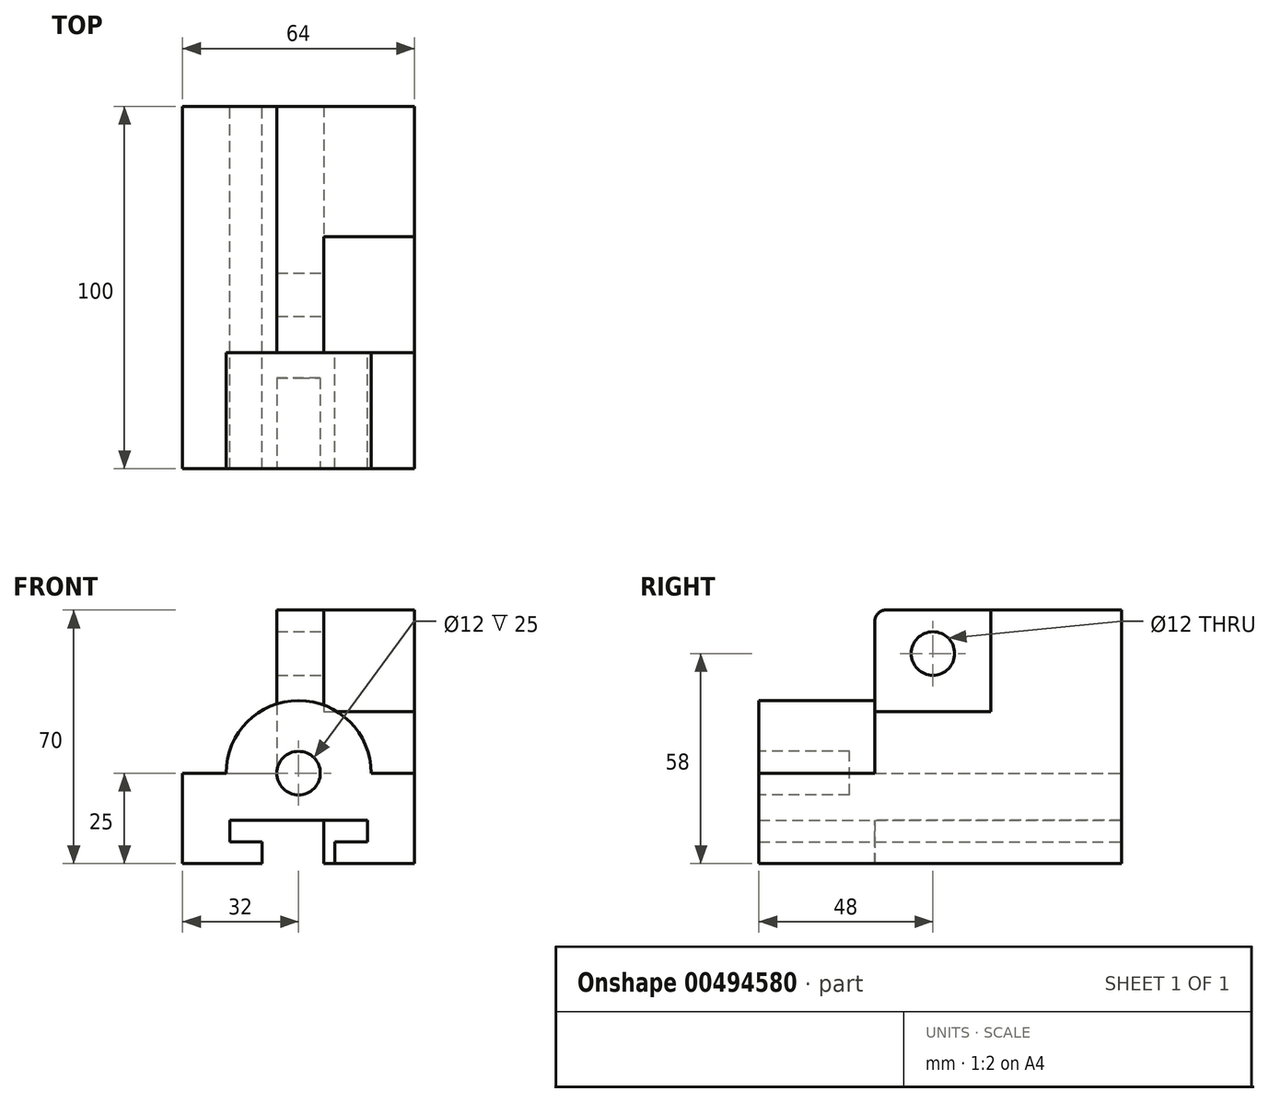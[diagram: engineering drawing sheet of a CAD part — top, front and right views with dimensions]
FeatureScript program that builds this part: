
annotation { "Feature Type Name" : "Feature", "Feature Type Description" : "" }
export const myFeature = defineFeature(function(context is Context, id is Id, definition is map)
    precondition{}
    {
        {
            var Q0;
            Q0=qCreatedBy(makeId("Front.planeOp"),FACE);
            var sketch = newSketch(context, id + "F0", { "sketchPlane" : qUnion([Q0])});
            skLineSegment(sketch, "E0.bottom", {"start": v(-32, 0) * mm, "end": v(-10, 0) * mm});
            skLineSegment(sketch, "E0.top", {"start": v(-32, 25) * mm, "end": v(32, 25) * mm});
            skLineSegment(sketch, "E0.left", {"start": v(-32, 0) * mm, "end": v(-32, 25) * mm});
            skLineSegment(sketch, "E0.right", {"start": v(32, 0) * mm, "end": v(32, 25) * mm});
            skLineSegment(sketch, "E1.left", {"start": v(-10, 0) * mm, "end": v(-10, 6) * mm});
            skLineSegment(sketch, "E1.right", {"start": v(10, 0) * mm, "end": v(10, 6) * mm});
            skLineSegment(sketch, "E2.bottom", {"start": v(19, 6) * mm, "end": v(10, 6) * mm});
            skLineSegment(sketch, "E2.top", {"start": v(19, 12) * mm, "end": v(-19, 12) * mm});
            skLineSegment(sketch, "E2.left", {"start": v(19, 6) * mm, "end": v(19, 12) * mm});
            skLineSegment(sketch, "E2.right", {"start": v(-19, 6) * mm, "end": v(-19, 12) * mm});
            skLineSegment(sketch, "E3.trimOffspring", {"start": v(-10, 6) * mm, "end": v(-19, 6) * mm});
            skLineSegment(sketch, "E4.trimOffspring", {"start": v(10, 0) * mm, "end": v(32, 0) * mm});
            skSolve(sketch);
        }
        {
            var Q0;
            Q0 = qSketchRegion(id + "F0", true);
            extrude(context, id + "F1", {"entities" : qUnion([Q0]), "endBound" : BoundingType.SYMMETRIC, "depth" : 100 * mm});
        }
        {
            var Q0;
            Q0=makeQuery(id+"F1.opExtrude","SWEPT_FACE",FACE,{"disambiguationData":[OSD([sQuery(id+"F0.wireOp",EDGE,"E0.right")])]});
            var sketch = newSketch(context, id + "F2", { "sketchPlane" : qUnion([Q0])});
            skLineSegment(sketch, "E5", {"start": v(50, 25) * mm, "end": v(50, 70) * mm});
            skLineSegment(sketch, "E6", {"start": v(50, 70) * mm, "end": v(14, 70) * mm});
            skLineSegment(sketch, "E7", {"start": v(14, 70) * mm, "end": v(14, 42) * mm});
            skLineSegment(sketch, "E8", {"start": v(14, 42) * mm, "end": v(-18, 42) * mm});
            skLineSegment(sketch, "E9", {"start": v(-18, 42) * mm, "end": v(-18, 25) * mm});
            skLineSegment(sketch, "E10", {"start": v(-18, 25) * mm, "end": v(-18, 0) * mm});
            skLineSegment(sketch, "E11", {"start": v(-18, 0) * mm, "end": v(50, 0) * mm});
            skLineSegment(sketch, "E12", {"start": v(50, 0) * mm, "end": v(50, 25) * mm});
            skSolve(sketch);
        }
        {
            var Q0;
            Q0 = qSketchRegion(id + "F2", true);
            extrude(context, id + "F3", {"entities" : qUnion([Q0]), "operationType" : NewBodyOperationType.ADD, "oppositeDirection" : true, "depth" : 25 * mm});
        }
        {
            var Q0;
            {var subQ0=sQuery(id+"F2.wireOp",EDGE,"E12");var subQ1=sQuery(id+"F2.wireOp",EDGE,"E5");var subQ2=sQuery(id+"F0.wireOp",EDGE,"E0.top");var subQ3=sQuery(id+"F2.wireOp",EDGE,"E6");var subQ4=sQuery(id+"F2.wireOp",EDGE,"E7");var subQ5=sQuery(id+"F2.wireOp",EDGE,"E8");var subQ6=sQuery(id+"F2.wireOp",EDGE,"E10");var subQ7=sQuery(id+"F2.wireOp",EDGE,"E9");Q0=makeQuery(id+"F3.boolean.opBoolean","SPLIT",FACE,{"disambiguationData":[TD([makeQuery(id+"F1.opExtrude","SWEPT_FACE",FACE,{"disambiguationData":[OSD([subQ2])]})])],"derivedFrom":makeQuery(id+"F3.opExtrude","CAP_FACE",FACE,{"disambiguationData":[OSD([subQ1,subQ3,subQ4,subQ5,subQ7,subQ6,sQuery(id+"F2.wireOp",EDGE,"E11"),subQ0])],"isStart":false})});}
            var sketch = newSketch(context, id + "F4", { "sketchPlane" : qUnion([Q0])});
            skLineSegment(sketch, "E13.bottom", {"start": v(-50, 25) * mm, "end": v(18, 25) * mm});
            skLineSegment(sketch, "E13.top", {"start": v(-50, 70) * mm, "end": v(18, 70) * mm});
            skLineSegment(sketch, "E13.left", {"start": v(-50, 25) * mm, "end": v(-50, 70) * mm});
            skLineSegment(sketch, "E13.right", {"start": v(18, 25) * mm, "end": v(18, 70) * mm});
            skCircle(sketch, "E14", {"center": v(2, 58) * mm, "radius": 6 * mm});
            skSolve(sketch);
        }
        {
            var Q0;
            Q0 = qSketchRegion(id + "F4", true);
            extrude(context, id + "F5", {"entities" : qUnion([Q0]), "operationType" : NewBodyOperationType.ADD, "depth" : 13 * mm});
        }
        {
            var Q0;
            Q0=makeQuery(id+"F5.opExtrude","SWEPT_EDGE",EDGE,{"disambiguationData":[OSD([sQuery(id+"F4.wireOp",EDGE,"E13.top"),sQuery(id+"F4.wireOp",EDGE,"E13.right")])]});
            fillet(context, id + "F6", {"entities" : qUnion([Q0]), "radius" : 3 * mm, "tangentPropagation" : true, "allowEdgeOverflow" : false});
        }
        {
            var Q0;
            Q0=makeQuery(id+"F1.opExtrude","CAP_FACE",FACE,{"disambiguationData":[OSD([sQuery(id+"F0.wireOp",EDGE,"E0.bottom"),sQuery(id+"F0.wireOp",EDGE,"E0.top"),sQuery(id+"F0.wireOp",EDGE,"E0.left"),sQuery(id+"F0.wireOp",EDGE,"E0.right"),sQuery(id+"F0.wireOp",EDGE,"E1.left"),sQuery(id+"F0.wireOp",EDGE,"E1.right"),sQuery(id+"F0.wireOp",EDGE,"E2.bottom"),sQuery(id+"F0.wireOp",EDGE,"E2.top"),sQuery(id+"F0.wireOp",EDGE,"E2.left"),sQuery(id+"F0.wireOp",EDGE,"E2.right"),sQuery(id+"F0.wireOp",EDGE,"E3.trimOffspring"),sQuery(id+"F0.wireOp",EDGE,"E4.trimOffspring")])],"isStart":false});
            var sketch = newSketch(context, id + "F7", { "sketchPlane" : qUnion([Q0])});
            skArc(sketch, "E15", {"start": v(20, 25) * mm, "mid": v(0, 45) * mm, "end": v(-20, 25) * mm});
            skCircle(sketch, "E16", {"center": v(0, 25) * mm, "radius": 6 * mm});
            skLineSegment(sketch, "E17", {"start": v(-20, 25) * mm, "end": v(20, 25) * mm});
            skSolve(sketch);
        }
        {
            var Q0;
            Q0 = qSketchRegion(id + "F7", true);
            extrude(context, id + "F8", {"entities" : qUnion([Q0]), "operationType" : NewBodyOperationType.ADD, "oppositeDirection" : true, "depth" : 32 * mm});
        }
        {
            var Q0;
            Q0=makeQuery(id+"F8.boolean.opBoolean","MERGE",FACE,{"derivedFrom":[makeQuery(id+"F1.opExtrude","CAP_FACE",FACE,{"disambiguationData":[OSD([sQuery(id+"F0.wireOp",EDGE,"E0.bottom"),sQuery(id+"F0.wireOp",EDGE,"E0.top"),sQuery(id+"F0.wireOp",EDGE,"E0.left"),sQuery(id+"F0.wireOp",EDGE,"E0.right"),sQuery(id+"F0.wireOp",EDGE,"E1.left"),sQuery(id+"F0.wireOp",EDGE,"E1.right"),sQuery(id+"F0.wireOp",EDGE,"E2.bottom"),sQuery(id+"F0.wireOp",EDGE,"E2.top"),sQuery(id+"F0.wireOp",EDGE,"E2.left"),sQuery(id+"F0.wireOp",EDGE,"E2.right"),sQuery(id+"F0.wireOp",EDGE,"E3.trimOffspring"),sQuery(id+"F0.wireOp",EDGE,"E4.trimOffspring")])],"isStart":false}),makeQuery(id+"F8.opExtrude","CAP_FACE",FACE,{"disambiguationData":[OSD([sQuery(id+"F7.wireOp",EDGE,"E15"),sQuery(id+"F7.wireOp",EDGE,"E16"),sQuery(id+"F7.wireOp",EDGE,"E17")])],"isStart":true})]});
            var sketch = newSketch(context, id + "F9", { "sketchPlane" : qUnion([Q0])});
            skCircle(sketch, "E18", {"center": v(0, 25) * mm, "radius": 6 * mm});
            skSolve(sketch);
        }
        {
            var Q0;
            Q0 = qSketchRegion(id + "F9", true);
            extrude(context, id + "F10", {"entities" : qUnion([Q0]), "operationType" : NewBodyOperationType.REMOVE, "oppositeDirection" : true, "depth" : 25 * mm});
        }
    });
